# Revit family: Haworth_Downtown_Chair_LowBack
name_source: partatom
category: Furniture
revit_build: Autodesk Revit 2018 (Build: 20170223_1515(x64)
units: mm (PartAtom-declared; Revit-internal decimal feet)

## family parameters
Always vertical = Yes
Cut with Voids When Loaded = No
OmniClass Number = 23.40.20.00
OmniClass Title = General Furniture and Specialties
Room Calculation Point = No
Shared = No
Work Plane-Based = No

## types (3) — shared parameters
Actual Depth = 2' - 2 1/4"
Actual Height = 2' - 11 3/4"
Actual Width = 2' - 3 1/4"
Assembly Code = E2020200
Description = Haworth Downtown Chair
Manufacturer = Haworth
Model = HCPF-DV4L
Size = Verify Final Dim. w/ Haworth
Trim Finish = Haworth _ Polymer _ Black
URL = http://www.haworth.com
URL - Product = http://www.haworth.com
Version = 3
Warranty = http://www.haworth.com

## per-type parameters (varying)
| type | Five Star Base | Managerial | Meeting | Visitor |
| HCPF-DM5L - Meeting | Yes | No | Yes | No |
| HCPF-DG5L - Managerial | Yes | Yes | No | No |
| HCPF-DV4L - Visitor | No | No | No | Yes |

## geometry (parser evidence)
native form markers: Blend x8, Sweep x5
no freeform markers — native parametric forms only
